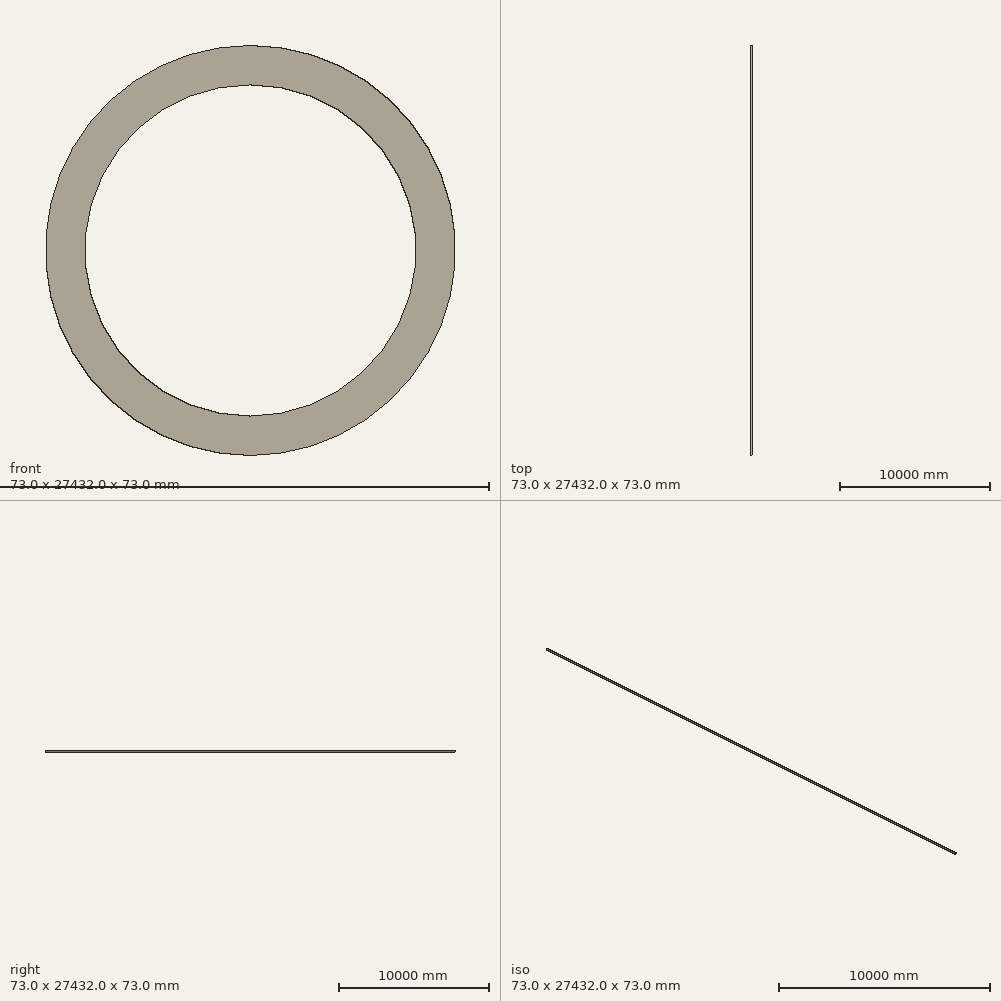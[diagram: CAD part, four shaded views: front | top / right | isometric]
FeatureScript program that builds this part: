
annotation { "Feature Type Name" : "Feature", "Feature Type Description" : "" }
export const myFeature = defineFeature(function(context is Context, id is Id, definition is map)
    precondition{}
    {
        {
            var Q0;
            Q0=qCreatedBy(makeId("Front.planeOp"),FACE);
            var sketch = newSketch(context, id + "F0", { "sketchPlane" : qUnion([Q0])});
            skCircle(sketch, "E0", {"center": v(0, 0) * mm, "radius": 36.51 * mm});
            skCircle(sketch, "E1", {"center": v(0, 0) * mm, "radius": 29.5 * mm});
            skSolve(sketch);
        }
        {
            var Q0;
            Q0=makeQuery(id+"F0.imprint","IMPRINT",FACE,{"disambiguationData":[TD([[makeQuery(id+"F0.imprint","IMPRINT",EDGE,{"derivedFrom":sQuery(id+"F0.wireOp",EDGE,"E0")}),1.0]])]});
            extrude(context, id + "F1", {"entities" : qUnion([Q0]), "endBound" : BoundingType.SYMMETRIC, "depth" : 27432 * mm});
        }
    });
